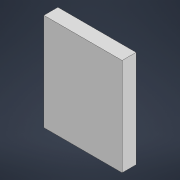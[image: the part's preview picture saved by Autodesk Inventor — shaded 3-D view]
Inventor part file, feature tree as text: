
AUTODESK INVENTOR PART (.ipt)
format: ipt  version: 2022 (Build 260153000, 153)  size: 84,992 bytes
history: native  units: mm
features: other x1, extrude x1, sketch x1
ambient origin geometry x8: Origin, YZ Plane, XZ Plane, XY Plane, X Axis, Y Axis, Z Axis, Center Point
bodies: Body1 (feature_tree)
feature tree (3):
  other  "Твердое тело1"
  extrude  "Выдавливание1"  Depth=246.0mm
  sketch  "Эскиз1"
